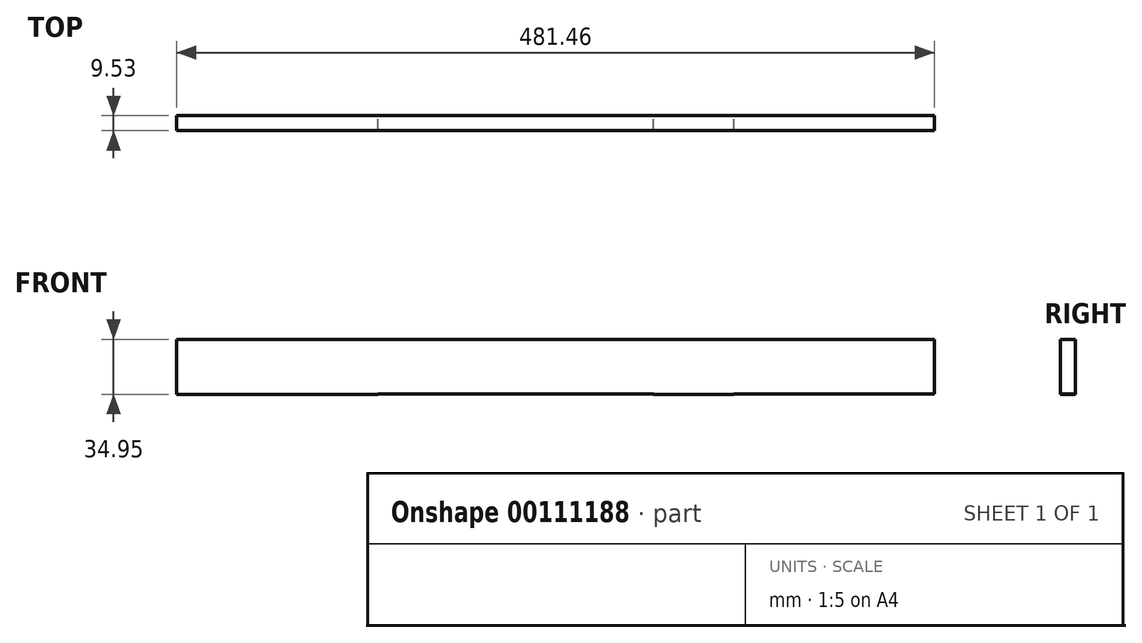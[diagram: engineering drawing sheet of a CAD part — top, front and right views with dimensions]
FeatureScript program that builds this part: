
annotation { "Feature Type Name" : "Feature", "Feature Type Description" : "" }
export const myFeature = defineFeature(function(context is Context, id is Id, definition is map)
    precondition{}
    {
        {
            var Q0;
            Q0=qCreatedBy(makeId("Front.planeOp"),FACE);
            var sketch = newSketch(context, id + "F0", { "sketchPlane" : qUnion([Q0])});
            skLineSegment(sketch, "E0.bottom", {"start": v(0, 0) * mm, "end": v(123.28, 0) * mm});
            skLineSegment(sketch, "E0.top", {"start": v(0, -34.9) * mm, "end": v(123.28, -34.9) * mm});
            skLineSegment(sketch, "E0.left", {"start": v(0, 0) * mm, "end": v(0, -34.9) * mm});
            skLineSegment(sketch, "E0.right", {"start": v(123.28, 0) * mm, "end": v(123.28, -34.9) * mm});
            skPoint(sketch, "E1.top.end.orphan", {"position": v(244.17, -34.9) * mm});
            skPoint(sketch, "E2.top.end.orphan", {"position": v(-51.6, -34.9) * mm});
            skLineSegment(sketch, "E3.bottom", {"start": v(0, 0) * mm, "end": v(-51.6, 0) * mm});
            skLineSegment(sketch, "E3.top", {"start": v(0, -34.9) * mm, "end": v(-51.6, -34.9) * mm});
            skLineSegment(sketch, "E3.right", {"start": v(-51.6, 0) * mm, "end": v(-51.6, -34.9) * mm});
            skLineSegment(sketch, "E4.bottom", {"start": v(123.28, 0) * mm, "end": v(174.41, 0) * mm});
            skLineSegment(sketch, "E4.top", {"start": v(123.28, -34.95) * mm, "end": v(174.41, -34.95) * mm});
            skLineSegment(sketch, "E4.left", {"start": v(123.28, 0) * mm, "end": v(123.28, -34.95) * mm});
            skLineSegment(sketch, "E4.right", {"start": v(174.41, 0) * mm, "end": v(174.41, -34.95) * mm});
            skLineSegment(sketch, "E5.top", {"start": v(-51.6, -34.95) * mm, "end": v(-179.67, -34.95) * mm});
            skLineSegment(sketch, "E5.left", {"start": v(-51.6, 0) * mm, "end": v(-51.6, -34.95) * mm});
            skLineSegment(sketch, "E5.right", {"start": v(-179.67, 0) * mm, "end": v(-179.67, -34.95) * mm});
            skLineSegment(sketch, "E6.left", {"start": v(-51.6, 0) * mm, "end": v(-51.6, 0) * mm});
            skLineSegment(sketch, "E6.right", {"start": v(-77.65, 0) * mm, "end": v(-77.65, 0) * mm});
            skLineSegment(sketch, "E7", {"start": v(-179.67, 0) * mm, "end": v(-51.6, 0) * mm});
            skLineSegment(sketch, "E8.left", {"start": v(174.41, 0) * mm, "end": v(174.41, -36.63) * mm});
            skLineSegment(sketch, "E9.left", {"start": v(174.41, 0) * mm, "end": v(174.41, -34.74) * mm});
            skLineSegment(sketch, "E10.bottom", {"start": v(174.41, 0) * mm, "end": v(301.79, 0) * mm});
            skLineSegment(sketch, "E10.top", {"start": v(174.41, -34.9) * mm, "end": v(301.79, -34.9) * mm});
            skLineSegment(sketch, "E10.left", {"start": v(174.41, 0) * mm, "end": v(174.41, -34.9) * mm});
            skLineSegment(sketch, "E10.right", {"start": v(301.79, 0) * mm, "end": v(301.79, -34.9) * mm});
            skSolve(sketch);
        }
        {
            var Q0;
            Q0 = qSketchRegion(id + "F0", true);
            extrude(context, id + "F1", {"entities" : qUnion([Q0]), "depth" : 9.52 * mm});
        }
    });
